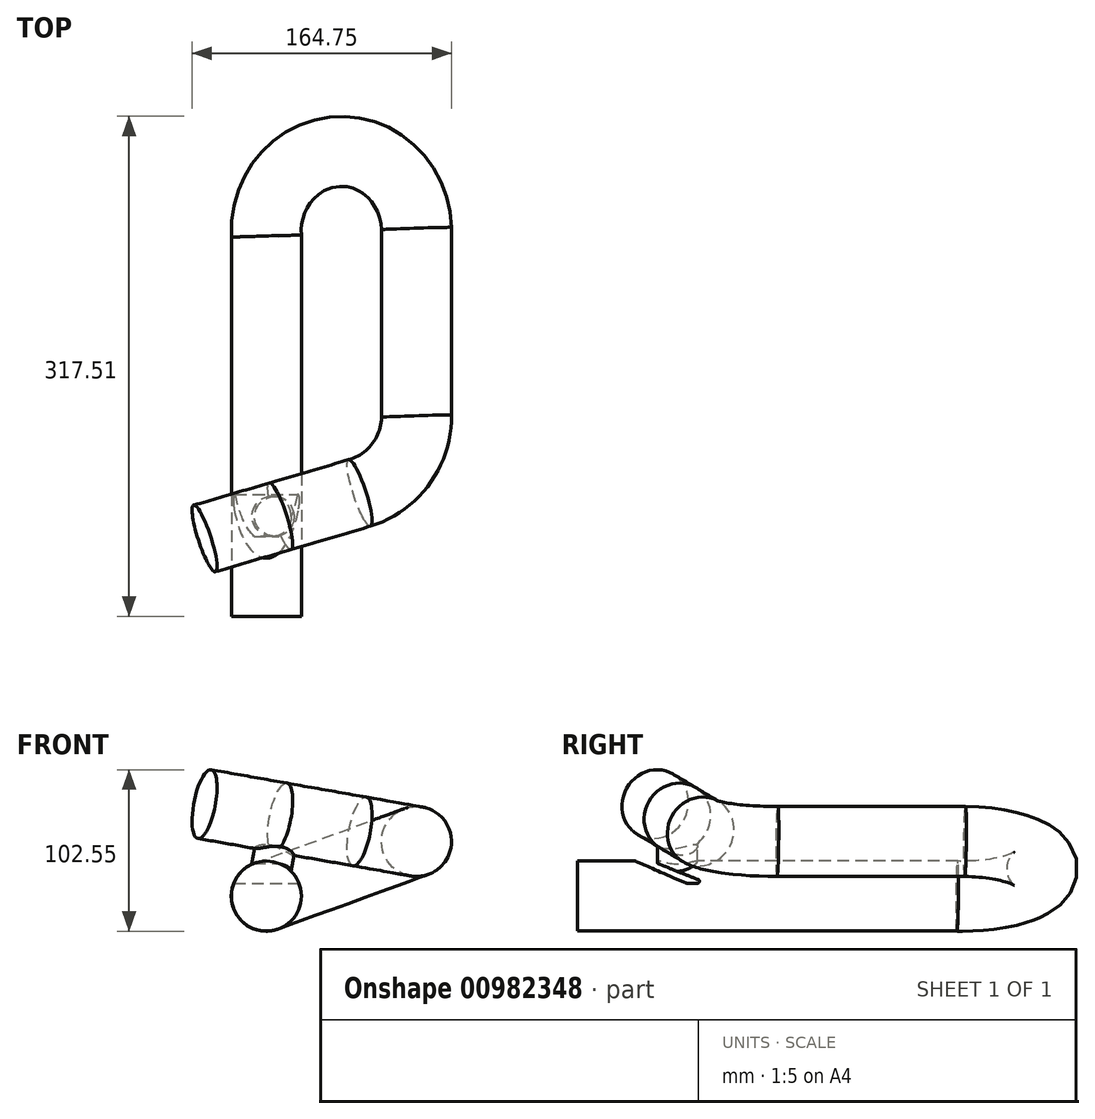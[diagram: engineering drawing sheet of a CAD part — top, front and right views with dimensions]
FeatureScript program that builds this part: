
annotation { "Feature Type Name" : "Feature", "Feature Type Description" : "" }
export const myFeature = defineFeature(function(context is Context, id is Id, definition is map)
    precondition{}
    {
        {
            var Q0;
            Q0=qCreatedBy(makeId("Top.planeOp"),FACE);
            var sketch = newSketch(context, id + "F0", { "sketchPlane" : qUnion([Q0])});
            skLineSegment(sketch, "E0", {"start": v(0, -63.5) * mm, "end": v(0, 177.8) * mm});
            skArc(sketch, "E1", {"start": v(101.6, 177.8) * mm, "mid": v(50.8, 228.6) * mm, "end": v(0, 177.8) * mm});
            skLineSegment(sketch, "E2", {"start": v(101.6, 177.8) * mm, "end": v(101.6, 76.2) * mm});
            skPoint(sketch, "E3", {"position": v(0, -38.1) * mm});
            skPoint(sketch, "E4", {"position": v(0, 25.4) * mm});
            skLineSegment(sketch, "E5", {"start": v(0, -63.5) * mm, "end": v(22.23, -63.5) * mm});
            skPoint(sketch, "E6", {"position": v(0, 0) * mm});
            skLineSegment(sketch, "E7", {"start": v(0, 0) * mm, "end": v(54.8, 14.93) * mm});
            skPoint(sketch, "E8.visualSharp", {"position": v(101.6, 27.7) * mm});
            skArc(sketch, "E8.filletArc", {"start": v(54.8, 14.93) * mm, "mid": v(88.56, 37.65) * mm, "end": v(101.6, 76.2) * mm});
            skLineSegment(sketch, "E9", {"start": v(0, 0) * mm, "end": v(-49.01, -13.36) * mm});
            skPoint(sketch, "E10", {"position": v(0, 76.2) * mm});
            skSolve(sketch);
        }
        {
            var Q0;
            Q0=qCreatedBy(makeId("Front.planeOp"),FACE);
            var Q1;
            Q1=sQuery(id+"F0.wireOp",VERTEX,"E0.start");
            cPlane(context, id + "F1", {"entities" : qUnion([Q0, Q1]), "cplaneType" : CPlaneType.PLANE_POINT, "offset" : 25.4 * mm, "width" : 152.4 * mm, "height" : 152.4 * mm});
        }
        {
            var Q0;
            Q0=qCreatedBy(id+"F1.planeOp",FACE);
            var sketch = newSketch(context, id + "F2", { "sketchPlane" : qUnion([Q0])});
            skPoint(sketch, "E11.0", {"position": v(0, 0) * mm});
            skLineSegment(sketch, "E12.0", {"start": v(0, 0) * mm, "end": v(22.23, 0) * mm});
            skCircle(sketch, "E13", {"center": v(0, 0) * mm, "radius": 22.23 * mm});
            skPoint(sketch, "E14", {"position": v(0, 22.23) * mm});
            skPoint(sketch, "E15", {"position": v(-22.23, 0) * mm});
            skPoint(sketch, "E16", {"position": v(0, -22.23) * mm});
            skSolve(sketch);
        }
        {
            var Q0;
            Q0=qCreatedBy(makeId("Front.planeOp"),FACE);
            var sketch = newSketch(context, id + "F3", { "sketchPlane" : qUnion([Q0])});
            skLineSegment(sketch, "E17", {"start": v(0, 0) * mm, "end": v(101.6, 36.98) * mm});
            skCircle(sketch, "E18.0", {"center": v(0, 0) * mm, "radius": 22.23 * mm});
            skPoint(sketch, "E19.0", {"position": v(101.6, 0) * mm});
            skSolve(sketch);
        }
        {
            var Q0;
            Q0=sQuery(id+"F0.wireOp",EDGE,"E0");
            var Q1;
            Q1=sQuery(id+"F3.wireOp",EDGE,"E17");
            cPlane(context, id + "F4", {"entities" : qUnion([Q0, Q1]), "cplaneType" : CPlaneType.LINE_ANGLE, "offset" : 25.4 * mm, "angle" : 0 * degree, "width" : 152.4 * mm, "height" : 152.4 * mm});
        }
        {
            var Q0;
            Q0=qCreatedBy(id+"F4.planeOp",FACE);
            var sketch = newSketch(context, id + "F5", { "sketchPlane" : qUnion([Q0])});
            skLineSegment(sketch, "E20.0", {"start": v(0, 63.5) * mm, "end": v(0, -177.8) * mm});
            skArc(sketch, "E21", {"start": v(0, -177.8) * mm, "mid": v(48.22, -231.72) * mm, "end": v(101.47, -182.76) * mm});
            skLineSegment(sketch, "E22", {"start": v(101.47, -182.76) * mm, "end": v(101.47, -25.4) * mm});
            skPoint(sketch, "E23.0", {"position": v(0, -25.4) * mm});
            skSolve(sketch);
        }
        {
            var Q0;
            Q0=qCreatedBy(id+"F1.planeOp",FACE);
            var sketch = newSketch(context, id + "F6", { "sketchPlane" : qUnion([Q0])});
            skPoint(sketch, "E24.0", {"position": v(95.35, 34.7) * mm});
            skLineSegment(sketch, "E25.0", {"start": v(0, 0) * mm, "end": v(95.35, 34.7) * mm});
            skLineSegment(sketch, "E26", {"start": v(95.35, 34.7) * mm, "end": v(0, 51.52) * mm});
            skSolve(sketch);
        }
        {
            var Q0;
            Q0=sQuery(id+"F6.wireOp",EDGE,"E26");
            var Q1;
            Q1=sQuery(id+"F5.wireOp",EDGE,"E22");
            cPlane(context, id + "F7", {"entities" : qUnion([Q0, Q1]), "cplaneType" : CPlaneType.LINE_ANGLE, "offset" : 25.4 * mm, "angle" : 0 * degree, "width" : 152.4 * mm, "height" : 152.4 * mm});
        }
        {
            var Q0;
            Q0=qCreatedBy(id+"F7.planeOp",FACE);
            var sketch = newSketch(context, id + "F8", { "sketchPlane" : qUnion([Q0])});
            skLineSegment(sketch, "E27.0", {"start": v(87.87, 182.76) * mm, "end": v(87.87, 63.6) * mm});
            skLineSegment(sketch, "E28", {"start": v(51.18, 14.8) * mm, "end": v(0, 0) * mm});
            skLineSegment(sketch, "E29", {"start": v(0, 0) * mm, "end": v(-48.8, -14.1) * mm});
            skArc(sketch, "E30", {"start": v(51.18, 14.8) * mm, "mid": v(77.68, 33.07) * mm, "end": v(87.87, 63.6) * mm});
            skLineSegment(sketch, "E31.0", {"start": v(0, -63.5) * mm, "end": v(0, 177.8) * mm});
            skCircle(sketch, "E32", {"center": v(0, 0) * mm, "radius": 12.7 * mm});
            skSolve(sketch);
        }
        {
            var Q0;
            Q0=makeQuery(id+"F3.imprint","IMPRINT",FACE,{"disambiguationData":[TD([[makeQuery(id+"F3.imprint","IMPRINT",EDGE,{"derivedFrom":sQuery(id+"F3.wireOp",EDGE,"E18.0")}),1.0]])]});
            var Q1;
            Q1=sQuery(id+"F0.wireOp",EDGE,"E0");
            var Q2;
            Q2=sQuery(id+"F5.wireOp",EDGE,"E21");
            sweep(context, id + "F9", {"profiles" : qUnion([Q0]), "path" : qUnion([Q1, Q2])});
        }
        {
            var Q0;
            Q0=makeQuery(id+"F9.opSweep","CAP_FACE",FACE,{"disambiguationData":[OSD([sQuery(id+"F3.wireOp",EDGE,"E18.0"),sQuery(id+"F5.wireOp",VERTEX,"E21.end")])],"isStart":true});
            var Q1;
            Q1=sQuery(id+"F8.wireOp",EDGE,"E27.0");
            var Q2;
            Q2=sQuery(id+"F8.wireOp",EDGE,"E30");
            var Q3;
            Q3=sQuery(id+"F8.wireOp",EDGE,"E28");
            var Q4;
            Q4=sQuery(id+"F8.wireOp",EDGE,"E29");
            sweep(context, id + "F10", {"operationType" : NewBodyOperationType.ADD, "profiles" : qUnion([Q0]), "path" : qUnion([Q1, Q2, Q3, Q4])});
        }
        {
            var Q0;
            {var subQ1=sQuery(id+"F8.wireOp",EDGE,"E28");var subQ3=sQuery(id+"F8.wireOp",EDGE,"E32");var subQ4=makeQuery(id+"F8.imprint","INTERSECT",VERTEX,{"derivedFrom":[subQ1,subQ3]});Q0=makeQuery(id+"F8.imprint","IMPRINT",FACE,{"disambiguationData":[TD([[makeQuery(id+"F8.imprint","IMPRINT",EDGE,{"disambiguationData":[TD([[subQ4,1.0]])],"derivedFrom":subQ3}),1.0]])]});}
            var Q1;
            {var subQ1=sQuery(id+"F8.wireOp",EDGE,"E28");var subQ3=sQuery(id+"F8.wireOp",EDGE,"E32");var subQ4=makeQuery(id+"F8.imprint","INTERSECT",VERTEX,{"derivedFrom":[subQ1,subQ3]});Q1=makeQuery(id+"F8.imprint","IMPRINT",FACE,{"disambiguationData":[TD([[makeQuery(id+"F8.imprint","IMPRINT",EDGE,{"disambiguationData":[TD([[subQ4,-1.0]])],"derivedFrom":subQ3}),1.0]])]});}
            var Q2;
            {var subQ1=sQuery(id+"F8.wireOp",EDGE,"E29");var subQ3=sQuery(id+"F8.wireOp",EDGE,"E32");var subQ4=makeQuery(id+"F8.imprint","INTERSECT",VERTEX,{"derivedFrom":[subQ1,subQ3]});Q2=makeQuery(id+"F8.imprint","IMPRINT",FACE,{"disambiguationData":[TD([[makeQuery(id+"F8.imprint","IMPRINT",EDGE,{"disambiguationData":[TD([[subQ4,1.0]])],"derivedFrom":subQ3}),1.0]])]});}
            var Q3;
            {var subQ1=sQuery(id+"F8.wireOp",EDGE,"E29");var subQ3=sQuery(id+"F8.wireOp",EDGE,"E32");var subQ4=makeQuery(id+"F8.imprint","INTERSECT",VERTEX,{"derivedFrom":[subQ1,subQ3]});Q3=makeQuery(id+"F8.imprint","IMPRINT",FACE,{"disambiguationData":[TD([[makeQuery(id+"F8.imprint","IMPRINT",EDGE,{"disambiguationData":[TD([[subQ4,-1.0]])],"derivedFrom":subQ3}),1.0]])]});}
            var Q4;
            Q4=sQuery(id+"F8.wireOp",EDGE,"E32");
            extrude(context, id + "F11", {"entities" : qUnion([Q0, Q1, Q2, Q3]), "operationType" : NewBodyOperationType.ADD, "surfaceEntities" : qUnion([Q4]), "oppositeDirection" : true, "depth" : 38.1 * mm, "offsetDistance" : 25.4 * mm});
        }
        {
            var Q0;
            Q0=qCreatedBy(makeId("Right.planeOp"),FACE);
            var sketch = newSketch(context, id + "F12", { "sketchPlane" : qUnion([Q0])});
            skLineSegment(sketch, "E33", {"start": v(-63.5, 22.23) * mm, "end": v(-26.64, 22.23) * mm});
            skLineSegment(sketch, "E34", {"start": v(-63.5, 22.23) * mm, "end": v(-27.77, 22.23) * mm});
            skLineSegment(sketch, "E35", {"start": v(177.54, -22.23) * mm, "end": v(-63.5, -22.23) * mm});
            skLineSegment(sketch, "E36", {"start": v(12.7, 26.64) * mm, "end": v(12.7, 25.01) * mm});
            skLineSegment(sketch, "E37", {"start": v(-12.7, 25.01) * mm, "end": v(-12.7, 26.63) * mm});
            skLineSegment(sketch, "E38", {"start": v(-12.7, 20.76) * mm, "end": v(13.63, 10.25) * mm});
            skLineSegment(sketch, "E39", {"start": v(13.88, 9.88) * mm, "end": v(13.88, 9.38) * mm});
            skLineSegment(sketch, "E40", {"start": v(12.6, 8.1) * mm, "end": v(7.04, 8.1) * mm});
            skLineSegment(sketch, "E41", {"start": v(4.5, 8.64) * mm, "end": v(-26.64, 22.22) * mm});
            skPoint(sketch, "E42.visualSharp", {"position": v(5.72, 8.1) * mm});
            skArc(sketch, "E42.filletArc", {"start": v(4.5, 8.64) * mm, "mid": v(5.75, 8.24) * mm, "end": v(7.04, 8.1) * mm});
            skPoint(sketch, "E43.visualSharp", {"position": v(13.88, 8.1) * mm});
            skArc(sketch, "E43.filletArc", {"start": v(12.6, 8.1) * mm, "mid": v(13.5, 8.48) * mm, "end": v(13.88, 9.38) * mm});
            skPoint(sketch, "E44.visualSharp", {"position": v(13.88, 10.15) * mm});
            skArc(sketch, "E44.filletArc", {"start": v(13.88, 9.88) * mm, "mid": v(13.81, 10.1) * mm, "end": v(13.63, 10.25) * mm});
            skLineSegment(sketch, "E45", {"start": v(-26.64, 22.22) * mm, "end": v(-26.64, 22.23) * mm});
            skLineSegment(sketch, "E46", {"start": v(-12.7, 21.89) * mm, "end": v(-12.7, 31.67) * mm});
            skLineSegment(sketch, "E47", {"start": v(177.57, -22.23) * mm, "end": v(-63.5, -22.23) * mm});
            skLineSegment(sketch, "E48", {"start": v(-12.7, 22.23) * mm, "end": v(-12.7, 20.76) * mm});
            skLineSegment(sketch, "E49", {"start": v(-12.7, 20.76) * mm, "end": v(-12.7, 22.23) * mm});
            skLineSegment(sketch, "E50.trimOffspring", {"start": v(-12.7, 22.23) * mm, "end": v(178.07, 22.23) * mm});
            skLineSegment(sketch, "E51.trimOffspring", {"start": v(-15.19, 22.23) * mm, "end": v(178.04, 22.23) * mm});
            skLineSegment(sketch, "E52", {"start": v(-15.19, 22.23) * mm, "end": v(-26.64, 22.23) * mm});
            skSolve(sketch);
        }
        {
            var Q0;
            Q0=makeQuery(id+"F12.imprint","IMPRINT",FACE,{"disambiguationData":[TD([[makeQuery(id+"F12.imprint","IMPRINT",EDGE,{"derivedFrom":sQuery(id+"F12.wireOp",EDGE,"E38")}),-1.0]])]});
            extrude(context, id + "F13", {"entities" : qUnion([Q0]), "operationType" : NewBodyOperationType.REMOVE, "endBound" : BoundingType.SYMMETRIC, "oppositeDirection" : true, "depth" : 50.8 * mm, "offsetDistance" : 25.4 * mm});
        }
    });
